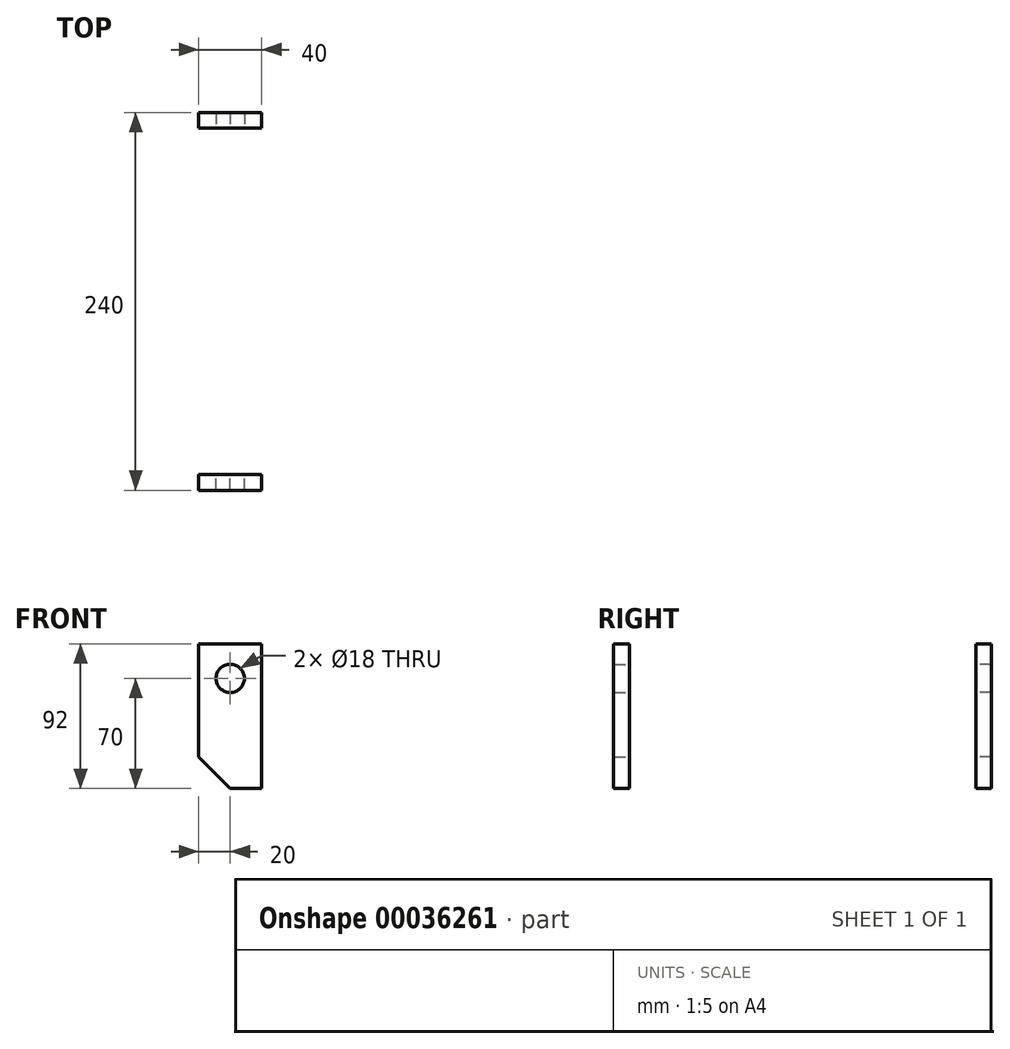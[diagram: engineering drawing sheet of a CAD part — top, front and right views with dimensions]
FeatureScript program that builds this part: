
annotation { "Feature Type Name" : "Feature", "Feature Type Description" : "" }
export const myFeature = defineFeature(function(context is Context, id is Id, definition is map)
    precondition{}
    {
        {
            var Q0;
            Q0=qCreatedBy(makeId("Front.planeOp"),FACE);
            var sketch = newSketch(context, id + "F0", { "sketchPlane" : qUnion([Q0])});
            skLineSegment(sketch, "E0", {"start": v(-20, 22) * mm, "end": v(20, 22) * mm});
            skLineSegment(sketch, "E1", {"start": v(20, 22) * mm, "end": v(20, -70) * mm});
            skLineSegment(sketch, "E2", {"start": v(20, -70) * mm, "end": v(0, -70) * mm});
            skLineSegment(sketch, "E3", {"start": v(0, -70) * mm, "end": v(-20, -50) * mm});
            skLineSegment(sketch, "E4", {"start": v(-20, -50) * mm, "end": v(-20, 22) * mm});
            skCircle(sketch, "E5", {"center": v(0, 0) * mm, "radius": 9 * mm});
            skSolve(sketch);
        }
        {
            var Q0;
            Q0 = qSketchRegion(id + "F0", true);
            extrude(context, id + "F1", {"entities" : qUnion([Q0]), "oppositeDirection" : true, "depth" : 10 * mm});
        }
        {
            var Q0;
            Q0=makeQuery(id+"F1.opExtrude","SWEPT_BODY",BODY,{"disambiguationData":[OSD([sQuery(id+"F0.wireOp",EDGE,"E0"),sQuery(id+"F0.wireOp",EDGE,"E1"),sQuery(id+"F0.wireOp",EDGE,"E2"),sQuery(id+"F0.wireOp",EDGE,"E3"),sQuery(id+"F0.wireOp",EDGE,"E4"),sQuery(id+"F0.wireOp",EDGE,"E5")])]});
            transform(context, id + "F2", {"entities" : qUnion([Q0]), "transformType" : TransformType.TRANSLATION_3D, "dx" : 0 * mm, "dy" : 10 * mm, "dz" : 0 * mm, "makeCopy" : false});
        }
        {
            var Q0;
            Q0=makeQuery(id+"F1.opExtrude","SWEPT_BODY",BODY,{"disambiguationData":[OSD([sQuery(id+"F0.wireOp",EDGE,"E0"),sQuery(id+"F0.wireOp",EDGE,"E1"),sQuery(id+"F0.wireOp",EDGE,"E2"),sQuery(id+"F0.wireOp",EDGE,"E3"),sQuery(id+"F0.wireOp",EDGE,"E4"),sQuery(id+"F0.wireOp",EDGE,"E5")])]});
            var Q1;
            Q1=qCreatedBy(makeId("Front.planeOp"),FACE);
            mirror(context, id + "F3", {"entities" : qUnion([Q0]), "mirrorPlane" : qUnion([Q1])});
        }
        {
            var Q0;
            Q0=makeQuery(id+"F3.opPattern","COPY",BODY,{"derivedFrom":makeQuery(id+"F1.opExtrude","SWEPT_BODY",BODY,{"disambiguationData":[OSD([sQuery(id+"F0.wireOp",EDGE,"E0"),sQuery(id+"F0.wireOp",EDGE,"E1"),sQuery(id+"F0.wireOp",EDGE,"E2"),sQuery(id+"F0.wireOp",EDGE,"E3"),sQuery(id+"F0.wireOp",EDGE,"E4"),sQuery(id+"F0.wireOp",EDGE,"E5")])]}),"instanceName":"1"});
            transform(context, id + "F4", {"entities" : qUnion([Q0]), "transformType" : TransformType.TRANSLATION_3D, "dx" : 0 * mm, "dy" : -200 * mm, "dz" : 0 * mm, "makeCopy" : false});
        }
    });
